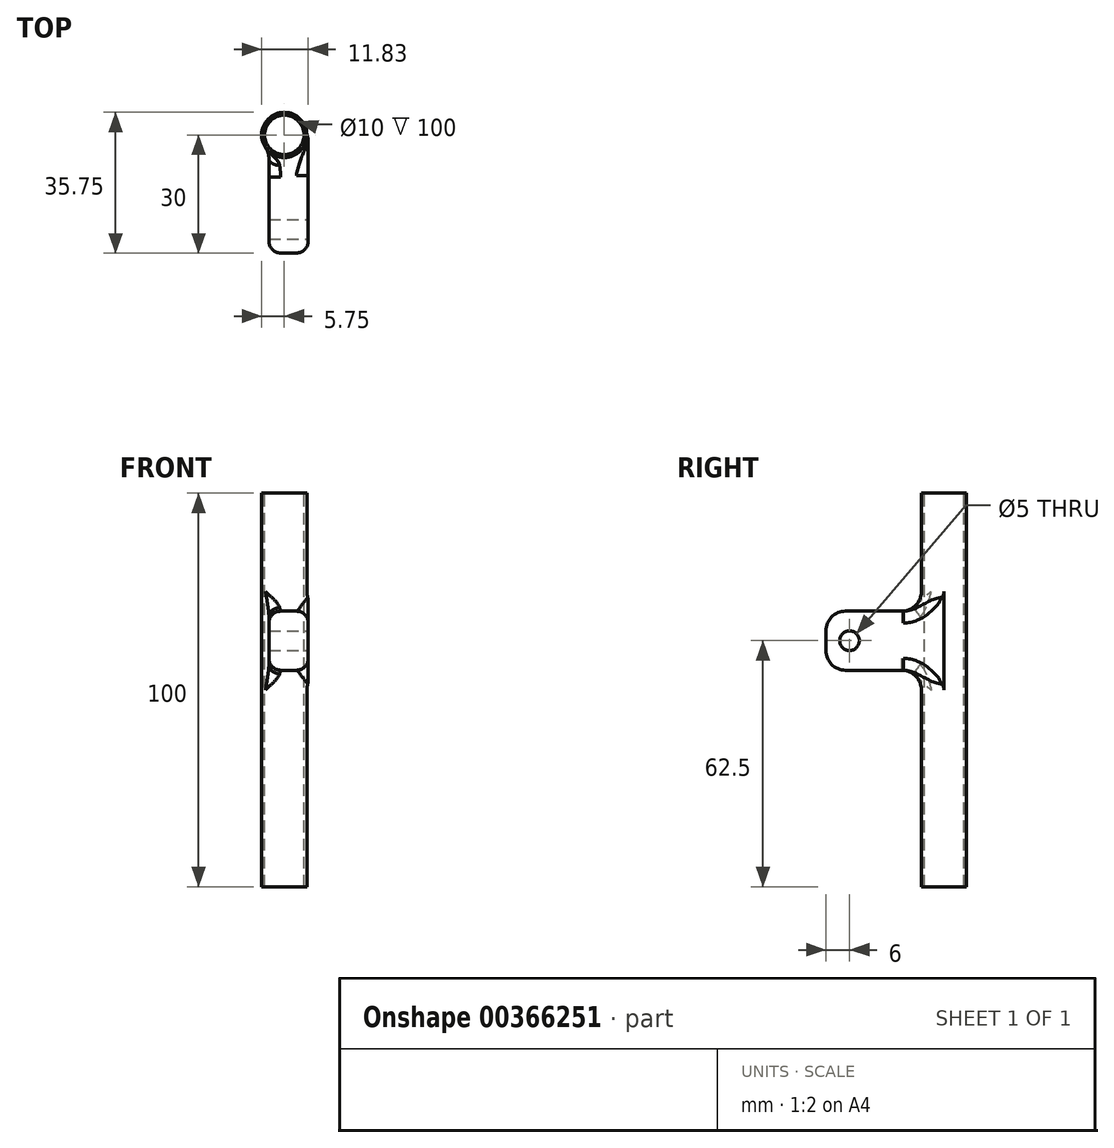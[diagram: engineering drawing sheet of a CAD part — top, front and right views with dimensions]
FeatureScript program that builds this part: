
annotation { "Feature Type Name" : "Feature", "Feature Type Description" : "" }
export const myFeature = defineFeature(function(context is Context, id is Id, definition is map)
    precondition{}
    {
        {
            var Q0;
            Q0=qCreatedBy(makeId("Top.planeOp"),FACE);
            var sketch = newSketch(context, id + "F0", { "sketchPlane" : qUnion([Q0])});
            skCircle(sketch, "E0", {"center": v(0, 0) * mm, "radius": 5.75 * mm});
            skSolve(sketch);
        }
        {
            var Q0;
            Q0=makeQuery(id+"F0.imprint","IMPRINT",FACE,{"disambiguationData":[TD([[makeQuery(id+"F0.imprint","IMPRINT",EDGE,{"derivedFrom":sQuery(id+"F0.wireOp",EDGE,"E0")}),1.0]])]});
            extrude(context, id + "F1", {"entities" : qUnion([Q0]), "depth" : 100 * mm});
        }
        {
            var Q0;
            Q0=qCreatedBy(makeId("Front.planeOp"),FACE);
            var sketch = newSketch(context, id + "F2", { "sketchPlane" : qUnion([Q0])});
            skLineSegment(sketch, "E1.bottom", {"start": v(-3.92, 70) * mm, "end": v(6.08, 70) * mm});
            skLineSegment(sketch, "E1.top", {"start": v(-3.92, 55) * mm, "end": v(6.08, 55) * mm});
            skLineSegment(sketch, "E1.left", {"start": v(-3.92, 70) * mm, "end": v(-3.92, 55) * mm});
            skLineSegment(sketch, "E1.right", {"start": v(6.08, 70) * mm, "end": v(6.08, 55) * mm});
            skSolve(sketch);
        }
        {
            var Q0;
            Q0 = qSketchRegion(id + "F2", true);
            extrude(context, id + "F3", {"entities" : qUnion([Q0]), "operationType" : NewBodyOperationType.ADD, "depth" : 30 * mm});
        }
        {
            var Q0;
            Q0=makeQuery(id+"F3.opExtrude","CAP_EDGE",EDGE,{"disambiguationData":[OSD([sQuery(id+"F2.wireOp",EDGE,"E1.bottom")])],"isStart":false});
            var Q1;
            Q1=makeQuery(id+"F3.opExtrude","CAP_EDGE",EDGE,{"disambiguationData":[OSD([sQuery(id+"F2.wireOp",EDGE,"E1.top")])],"isStart":false});
            var Q2;
            Q2=makeQuery(id+"F3.boolean.opBoolean","INTERSECT",EDGE,{"derivedFrom":[makeQuery(id+"F1.opExtrude","SWEPT_FACE",FACE,{"disambiguationData":[OSD([sQuery(id+"F0.wireOp",EDGE,"E0")])]}),makeQuery(id+"F3.opExtrude","SWEPT_FACE",FACE,{"disambiguationData":[OSD([sQuery(id+"F2.wireOp",EDGE,"E1.right")])]})]});
            var Q3;
            Q3=makeQuery(id+"F3.boolean.opBoolean","INTERSECT",EDGE,{"derivedFrom":[makeQuery(id+"F1.opExtrude","SWEPT_FACE",FACE,{"disambiguationData":[OSD([sQuery(id+"F0.wireOp",EDGE,"E0")])]}),makeQuery(id+"F3.opExtrude","SWEPT_FACE",FACE,{"disambiguationData":[OSD([sQuery(id+"F2.wireOp",EDGE,"E1.left")])]})]});
            var Q4;
            Q4=makeQuery(id+"F3.boolean.opBoolean","INTERSECT",EDGE,{"derivedFrom":[makeQuery(id+"F1.opExtrude","SWEPT_FACE",FACE,{"disambiguationData":[OSD([sQuery(id+"F0.wireOp",EDGE,"E0")])]}),makeQuery(id+"F3.opExtrude","SWEPT_FACE",FACE,{"disambiguationData":[OSD([sQuery(id+"F2.wireOp",EDGE,"E1.bottom")])]})]});
            var Q5;
            Q5=makeQuery(id+"F3.boolean.opBoolean","INTERSECT",EDGE,{"derivedFrom":[makeQuery(id+"F1.opExtrude","SWEPT_FACE",FACE,{"disambiguationData":[OSD([sQuery(id+"F0.wireOp",EDGE,"E0")])]}),makeQuery(id+"F3.opExtrude","SWEPT_FACE",FACE,{"disambiguationData":[OSD([sQuery(id+"F2.wireOp",EDGE,"E1.top")])]})]});
            fillet(context, id + "F4", {"entities" : qUnion([Q0, Q1, Q2, Q3, Q4, Q5]), "radius" : 5 * mm, "tangentPropagation" : true, "allowEdgeOverflow" : false});
        }
        {
            var Q0;
            Q0=makeQuery(id+"F1.opExtrude","CAP_FACE",FACE,{"disambiguationData":[OSD([sQuery(id+"F0.wireOp",EDGE,"E0")])],"isStart":false});
            var sketch = newSketch(context, id + "F5", { "sketchPlane" : qUnion([Q0])});
            skCircle(sketch, "E2", {"center": v(0, 0) * mm, "radius": 5 * mm});
            skSolve(sketch);
        }
        {
            var Q0;
            Q0 = qSketchRegion(id + "F5", true);
            extrude(context, id + "F6", {"entities" : qUnion([Q0]), "operationType" : NewBodyOperationType.REMOVE, "endBound" : BoundingType.THROUGH_ALL, "oppositeDirection" : true, "depth" : 25 * mm});
        }
        {
            var Q0;
            Q0=makeQuery(id+"F3.opExtrude","SWEPT_EDGE",EDGE,{"disambiguationData":[OSD([sQuery(id+"F2.wireOp",EDGE,"E1.top"),sQuery(id+"F2.wireOp",EDGE,"E1.right")])]});
            var Q1;
            Q1=makeQuery(id+"F3.opExtrude","SWEPT_FACE",FACE,{"disambiguationData":[OSD([sQuery(id+"F2.wireOp",EDGE,"E1.left")])]});
            var Q2;
            Q2=makeQuery(id+"F3.opExtrude","SWEPT_FACE",FACE,{"disambiguationData":[OSD([sQuery(id+"F2.wireOp",EDGE,"E1.bottom")])]});
            var Q3;
            Q3=makeQuery(id+"F3.opExtrude","SWEPT_FACE",FACE,{"disambiguationData":[OSD([sQuery(id+"F2.wireOp",EDGE,"E1.top")])]});
            var Q4;
            Q4=makeQuery(id+"F3.opExtrude","SWEPT_FACE",FACE,{"disambiguationData":[OSD([sQuery(id+"F2.wireOp",EDGE,"E1.right")])]});
            fillet(context, id + "F7", {"entities" : qUnion([Q0, Q1, Q2, Q3, Q4]), "radius" : 3 * mm, "tangentPropagation" : true, "allowEdgeOverflow" : false});
        }
        {
            var Q0;
            Q0=makeQuery(id+"F3.opExtrude","SWEPT_FACE",FACE,{"disambiguationData":[OSD([sQuery(id+"F2.wireOp",EDGE,"E1.right")])]});
            var sketch = newSketch(context, id + "F8", { "sketchPlane" : qUnion([Q0])});
            skPoint(sketch, "E3.centerSnap0", {"position": v(-17.65, 67) * mm});
            skCircle(sketch, "E4", {"center": v(-24, 62.5) * mm, "radius": 2.5 * mm});
            skSolve(sketch);
        }
        {
            var Q0;
            Q0 = qSketchRegion(id + "F8", true);
            extrude(context, id + "F9", {"entities" : qUnion([Q0]), "operationType" : NewBodyOperationType.REMOVE, "endBound" : BoundingType.THROUGH_ALL, "oppositeDirection" : true, "depth" : 25 * mm});
        }
    });
